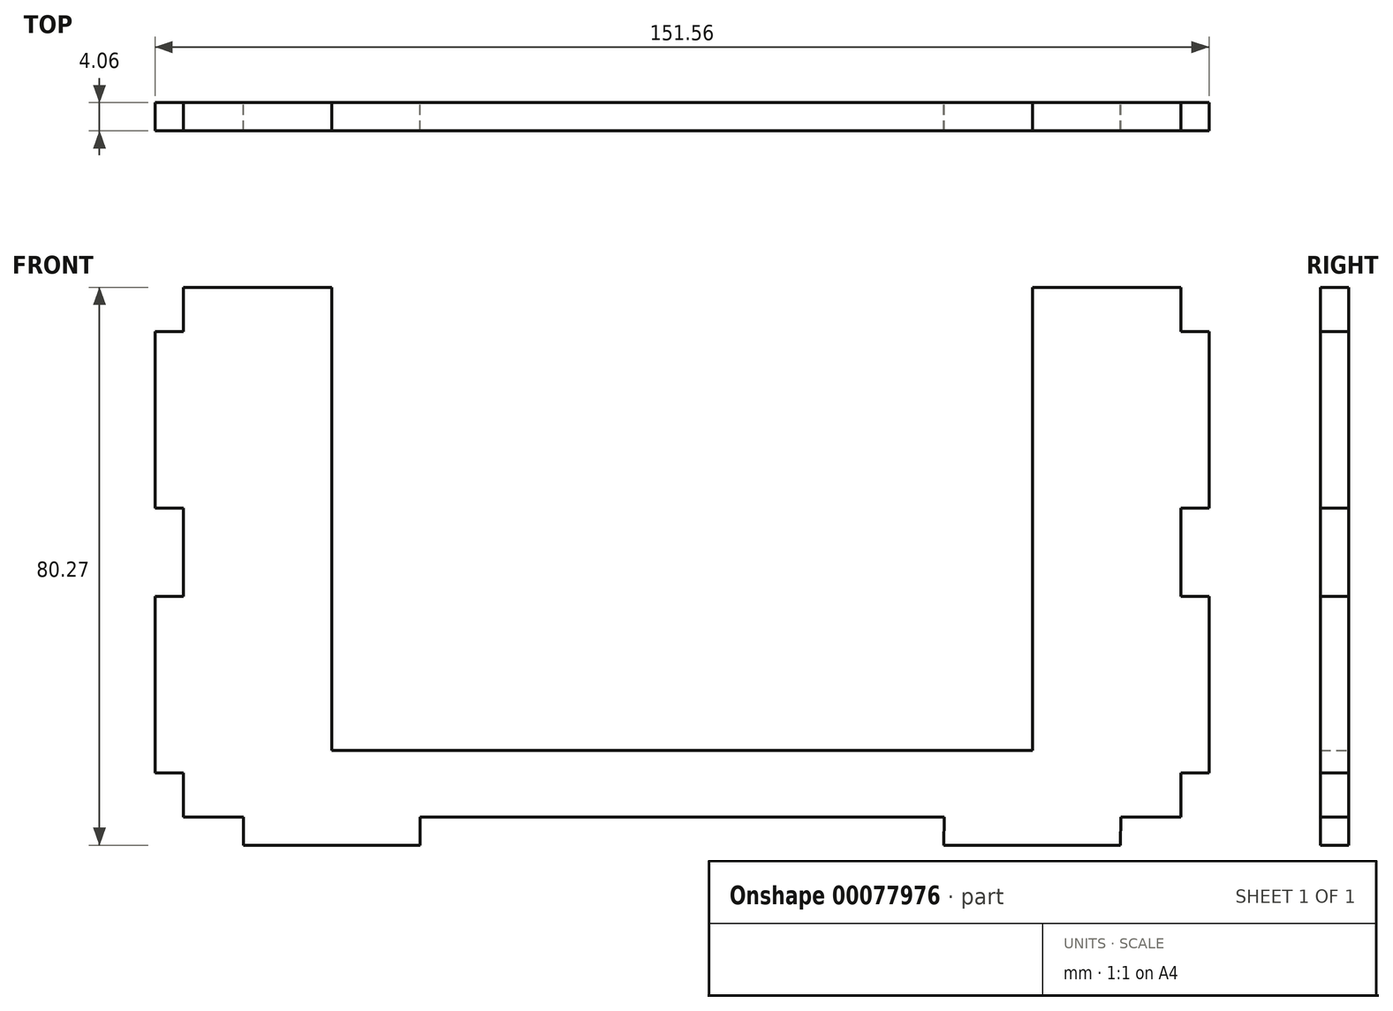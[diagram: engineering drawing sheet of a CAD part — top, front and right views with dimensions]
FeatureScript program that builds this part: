
annotation { "Feature Type Name" : "Feature", "Feature Type Description" : "" }
export const myFeature = defineFeature(function(context is Context, id is Id, definition is map)
    precondition{}
    {
        {
            var Q0;
            Q0=qCreatedBy(makeId("Front.planeOp"),FACE);
            var sketch = newSketch(context, id + "F0", { "sketchPlane" : qUnion([Q0])});
            skLineSegment(sketch, "E0.bottom", {"start": v(-78.32, 59.56) * mm, "end": v(-71.97, 59.56) * mm});
            skLineSegment(sketch, "E0.top", {"start": v(-46.56, -16.64) * mm, "end": v(-43.36, -16.64) * mm});
            skPoint(sketch, "E1.orphan", {"position": v(54.19, -16.64) * mm});
            skPoint(sketch, "E2.orphan", {"position": v(-43.36, -16.64) * mm});
            skPoint(sketch, "E3.orphan", {"position": v(-8.89, 59.56) * mm});
            skLineSegment(sketch, "E4.trimOffspring", {"start": v(-17.96, -16.64) * mm, "end": v(28.79, -16.64) * mm});
            skPoint(sketch, "E5.end.orphan", {"position": v(-8.89, -16.64) * mm});
            skPoint(sketch, "E5.start.orphan", {"position": v(-8.89, -20) * mm});
            skLineSegment(sketch, "E6", {"start": v(-8.89, 59.56) * mm, "end": v(-8.89, -16.64) * mm});
            skLineSegment(sketch, "E7", {"start": v(-71.97, 59.56) * mm, "end": v(-65.62, 59.56) * mm});
            skPoint(sketch, "E7.endSnap0", {"position": v(-78.32, 59.56) * mm});
            skLineSegment(sketch, "E8", {"start": v(-84.67, 27.8) * mm, "end": v(-80.6, 27.8) * mm});
            skLineSegment(sketch, "E9.bottom", {"start": v(-84.67, 53.2) * mm, "end": v(-80.6, 53.2) * mm});
            skLineSegment(sketch, "E9.left", {"start": v(-84.67, 53.2) * mm, "end": v(-84.67, 27.8) * mm});
            skLineSegment(sketch, "E10", {"start": v(-84.67, 15.1) * mm, "end": v(-80.6, 15.1) * mm});
            skLineSegment(sketch, "E11.bottom", {"start": v(-80.6, 15.1) * mm, "end": v(-84.67, 15.1) * mm});
            skLineSegment(sketch, "E11.top", {"start": v(-80.6, -10.3) * mm, "end": v(-84.67, -10.3) * mm});
            skLineSegment(sketch, "E11.right", {"start": v(-84.67, 15.1) * mm, "end": v(-84.67, -10.3) * mm});
            skLineSegment(sketch, "E12", {"start": v(-80.6, -10.3) * mm, "end": v(-80.6, -16.64) * mm});
            skLineSegment(sketch, "E13", {"start": v(-80.6, 15.1) * mm, "end": v(-80.6, 27.8) * mm});
            skLineSegment(sketch, "E14", {"start": v(-80.6, 53.2) * mm, "end": v(-80.6, 59.56) * mm});
            skPoint(sketch, "E15.end.orphan", {"position": v(-84.67, 59.56) * mm});
            skPoint(sketch, "E16.start.orphan", {"position": v(-88.73, 61.34) * mm});
            skPoint(sketch, "E17.0.end.orphan", {"position": v(-88.73, 35.94) * mm});
            skLineSegment(sketch, "E18", {"start": v(-80.6, 59.56) * mm, "end": v(-65.62, 59.56) * mm});
            skPoint(sketch, "E19.orphan", {"position": v(-84.67, -16.64) * mm});
            skPoint(sketch, "E20.0.end.orphan", {"position": v(-88.73, -10.3) * mm});
            skPoint(sketch, "E21.0.end.orphan", {"position": v(-88.73, 15.1) * mm});
            skPoint(sketch, "E22.MirrorCS.end.orphan", {"position": v(70.95, 61.34) * mm});
            skPoint(sketch, "E23.MirrorCS.end.orphan", {"position": v(70.95, 35.94) * mm});
            skPoint(sketch, "E24.end.orphan", {"position": v(66.89, 53.2) * mm});
            skPoint(sketch, "E25.trimOffspring.end.orphan", {"position": v(66.89, 59.56) * mm});
            skPoint(sketch, "E26.trimOffspring.start.orphan", {"position": v(66.89, 27.8) * mm});
            skPoint(sketch, "E27.MirrorCS.end.orphan", {"position": v(70.95, 15.1) * mm});
            skPoint(sketch, "E27.MirrorCS.start.orphan", {"position": v(66.89, 15.1) * mm});
            skPoint(sketch, "E28.MirrorCS.end.orphan", {"position": v(70.95, -10.3) * mm});
            skLineSegment(sketch, "E29.MirrorCS", {"start": v(62.82, 15.1) * mm, "end": v(62.82, 27.8) * mm});
            skLineSegment(sketch, "E30.MirrorCS", {"start": v(66.89, 15.1) * mm, "end": v(66.89, -10.3) * mm});
            skLineSegment(sketch, "E31.MirrorCS", {"start": v(66.89, 15.1) * mm, "end": v(62.82, 15.1) * mm});
            skLineSegment(sketch, "E32.MirrorCS", {"start": v(62.82, -10.3) * mm, "end": v(66.89, -10.3) * mm});
            skLineSegment(sketch, "E33.MirrorCS", {"start": v(62.82, -10.3) * mm, "end": v(62.82, -16.64) * mm});
            skLineSegment(sketch, "E34.MirrorCS", {"start": v(66.89, 27.8) * mm, "end": v(62.82, 27.8) * mm});
            skLineSegment(sketch, "E35.MirrorCS", {"start": v(66.89, 53.2) * mm, "end": v(66.89, 27.8) * mm});
            skLineSegment(sketch, "E36.MirrorCS", {"start": v(66.89, 53.2) * mm, "end": v(62.82, 53.2) * mm});
            skLineSegment(sketch, "E37.MirrorCS", {"start": v(62.82, 53.2) * mm, "end": v(62.82, 59.56) * mm});
            skLineSegment(sketch, "E38.MirrorCS", {"start": v(62.82, 59.56) * mm, "end": v(47.84, 59.56) * mm});
            skPoint(sketch, "E39.orphan", {"position": v(54.19, -20) * mm});
            skPoint(sketch, "E40.orphan", {"position": v(-71.97, -20) * mm});
            skPoint(sketch, "E41.orphan", {"position": v(66.89, -16.64) * mm});
            skPoint(sketch, "E42.trimOffspring.start.orphan", {"position": v(66.89, -10.3) * mm});
            skLineSegment(sketch, "E43", {"start": v(28.79, -16.64) * mm, "end": v(-43.36, -16.64) * mm});
            skLineSegment(sketch, "E44.0", {"start": v(54.19, -21.4) * mm, "end": v(54.18, -21.4) * mm});
            skPoint(sketch, "E45.orphan", {"position": v(-70.15, -16.64) * mm});
            skLineSegment(sketch, "E46", {"start": v(-8.89, -16.64) * mm, "end": v(-8.89, -30.51) * mm});
            skLineSegment(sketch, "E47.0", {"start": v(-46.56, -20.7) * mm, "end": v(-71.96, -20.7) * mm});
            skLineSegment(sketch, "E48", {"start": v(-46.56, -20.7) * mm, "end": v(-46.56, -16.64) * mm});
            skLineSegment(sketch, "E49", {"start": v(-71.96, -20.7) * mm, "end": v(-71.96, -16.64) * mm});
            skLineSegment(sketch, "E50", {"start": v(-71.96, -16.64) * mm, "end": v(-80.6, -16.64) * mm});
            skPoint(sketch, "E51.trimOffspring.end.orphan", {"position": v(-80.6, -21.4) * mm});
            skPoint(sketch, "E52.end.orphan", {"position": v(-71.96, -21.4) * mm});
            skPoint(sketch, "E53.end.orphan", {"position": v(-71.96, -25.47) * mm});
            skPoint(sketch, "E54.end.orphan", {"position": v(-46.56, -25.47) * mm});
            skPoint(sketch, "E55.orphan", {"position": v(-65.62, -16.64) * mm});
            skPoint(sketch, "E56.start.orphan", {"position": v(-46.56, -21.4) * mm});
            skLineSegment(sketch, "E57.0", {"start": v(28.78, -20.7) * mm, "end": v(54.18, -20.7) * mm});
            skLineSegment(sketch, "E58", {"start": v(28.78, -20.7) * mm, "end": v(28.79, -16.64) * mm});
            skLineSegment(sketch, "E59", {"start": v(54.18, -20.7) * mm, "end": v(54.19, -16.64) * mm});
            skLineSegment(sketch, "E60", {"start": v(54.19, -16.64) * mm, "end": v(62.82, -16.64) * mm});
            skPoint(sketch, "E61.orphan", {"position": v(62.82, -21.4) * mm});
            skPoint(sketch, "E62.MirrorCS.start.orphan", {"position": v(54.18, -25.47) * mm});
            skPoint(sketch, "E63.MirrorCS.start.orphan", {"position": v(28.78, -25.47) * mm});
            skPoint(sketch, "E64.MirrorCS.start.orphan", {"position": v(28.78, -21.4) * mm});
            skLineSegment(sketch, "E65.0", {"start": v(41.49, -7.1) * mm, "end": v(-43.36, -7.1) * mm});
            skLineSegment(sketch, "E66", {"start": v(-59.27, -7.1) * mm, "end": v(41.49, -7.1) * mm});
            skLineSegment(sketch, "E67.0", {"start": v(-59.27, 59.56) * mm, "end": v(-59.27, -7.1) * mm});
            skLineSegment(sketch, "E68.0", {"start": v(41.49, 59.56) * mm, "end": v(41.49, -7.1) * mm});
            skLineSegment(sketch, "E69", {"start": v(-65.62, 59.56) * mm, "end": v(-59.27, 59.56) * mm});
            skLineSegment(sketch, "E70", {"start": v(41.49, 59.56) * mm, "end": v(47.84, 59.56) * mm});
            skPoint(sketch, "E71.end.orphan", {"position": v(-65.62, -7.1) * mm});
            skSolve(sketch);
        }
        {
            var Q0;
            {var subQ0=sQuery(id+"F0.wireOp",EDGE,"E0.top");Q0=makeQuery(id+"F0.imprint","IMPRINT",FACE,{"disambiguationData":[TD([[makeQuery(id+"F0.imprint","IMPRINT",EDGE,{"derivedFrom":subQ0}),1.0]])]});}
            var Q1;
            Q1=makeQuery(id+"F0.imprint","IMPRINT",FACE,{"disambiguationData":[TD([[makeQuery(id+"F0.imprint","IMPRINT",EDGE,{"derivedFrom":sQuery(id+"F0.wireOp",EDGE,"E30.MirrorCS")}),-1.0]])]});
            extrude(context, id + "F1", {"entities" : qUnion([Q0, Q1]), "depth" : 4.06 * mm});
        }
    });
